# Revit family: QMX_Vertical
name_source: partatom
category: Mechanical Equipment
units: mm (PartAtom-declared; Revit-internal decimal feet)

## family parameters
Always vertical = Yes
Cut with Voids When Loaded = No
Part Type = Normal
Room Calculation Point = No
Round Connector Dimension = Use Radius
Shared = No
Work Plane-Based = No

## types (18) — shared parameters
0 = 0' - 0"
1.5 = 0' - 1 1/2"
1.9375 = 0' - 1 15/16"
3 = 0' - 3"
45 = 45.00°
Manufacturer = Loren Cook Company
Model = QMX-Vertical
ONE EIGTH = 0' - 0 1/8"
Type Comments = Mixed Flow Inline Vertical Mount Belt Drive Arrangement 9
URL = www.lorencook.com

## per-type parameters (varying)
- 90-QMX_VER: (A/2)-.125=0' - 6 9/32"; (F+3)/2=0' - 7 11/16"; (G/2)-.75=0' - 8 7/16"; -(B/2)=-0' - 9 15/16"; -(G/2)-.75=-0' - 8 7/16"; A=1' - 0 13/16"; A/2=0' - 6 13/32"; A/4=0' - 3 7/32"; A/8=0' - 1 19/32"; B=1' - 7 7/8"; B/10=0' - 2"; B/2=0' - 9 15/16"; B/3*2=1' - 1 1/4"; B/6=0' - 3 5/16"; B/8=0' - 3 5/16"; BRACKET=0' - 3"; BRACKET/2=0' - 1 1/2"; C=1' - 3 7/8"; C/2=0' - 7 15/16"; D=0' - 8 1/2"; E=2' - 7 1/4"; E-D=1' - 10 3/4"; E-D-1.5=1' - 9 1/4"; F=1' - 0 3/8"; F+1.5=1' - 1 7/8"; F-1.5=0' - 10 7/8"; F/2=0' - 6 3/16"; G=1' - 6 3/8"; G+1.5=1' - 7 7/8"; G/2=0' - 9 3/16"; H=0' - 0 1/2"; H/2=0' - 0 1/4"; MC/2=0' - 6"; hole=0' - 6 25/32"; hole_dia=1' - 7 3/16"
- 120-QMX_VER: (A/2)-.125=0' - 8 13/32"; (F+3)/2=0' - 9 1/4"; (G/2)-.75=0' - 10 1/2"; -(B/2)=-1' - 0"; -(G/2)-.75=-0' - 10 1/2"; A=1' - 5 1/16"; A/2=0' - 8 17/32"; A/4=0' - 4 9/32"; A/8=0' - 2 1/8"; B=2' - 0"; B/10=0' - 2 13/32"; B/2=1' - 0"; B/3*2=1' - 4"; B/6=0' - 4"; B/8=0' - 4"; BRACKET=0' - 3"; BRACKET/2=0' - 1 1/2"; C=1' - 8 1/16"; C/2=0' - 10 1/32"; D=0' - 10 1/2"; E=3' - 0 11/16"; E-D=2' - 2 3/16"; E-D-1.5=2' - 0 11/16"; F=1' - 3 1/2"; F+1.5=1' - 5"; F-1.5=1' - 2"; F/2=0' - 7 3/4"; G=1' - 10 1/2"; G+1.5=2' - 0"; G/2=0' - 11 1/4"; H=0' - 0 1/2"; H/2=0' - 0 1/4"; MC/2=0' - 8"; hole=0' - 8 11/32"; hole_dia=1' - 11 9/16"
- 135-QMX_VER: (A/2)-.125=0' - 9 1/2"; (F+3)/2=0' - 10 1/4"; (G/2)-.75=1' - 0"; -(B/2)=-1' - 1 1/2"; -(G/2)-.75=-1' - 0"; A=1' - 7 1/4"; A/2=0' - 9 5/8"; A/4=0' - 4 13/16"; A/8=0' - 2 13/32"; B=2' - 3"; B/10=0' - 2 11/16"; B/2=1' - 1 1/2"; B/3*2=1' - 6"; B/6=0' - 4 1/2"; B/8=0' - 4 1/2"; BRACKET=0' - 3"; BRACKET/2=0' - 1 1/2"; C=1' - 10 1/4"; C/2=0' - 11 1/8"; D=1' - 0"; E=3' - 3 1/2"; E-D=2' - 3 1/2"; E-D-1.5=2' - 2"; F=1' - 5 1/2"; F+1.5=1' - 7"; F-1.5=1' - 4"; F/2=0' - 8 3/4"; G=2' - 1 1/2"; G+1.5=2' - 3"; G/2=1' - 0 3/4"; H=0' - 0 1/2"; H/2=0' - 0 1/4"; MC/2=0' - 9"; hole=0' - 9 1/8"; hole_dia=2' - 1 13/16"
- 150-QMX_VER: (A/2)-.125=0' - 10 9/16"; (F+3)/2=0' - 10 7/8"; (G/2)-.75=1' - 1 9/16"; -(B/2)=-1' - 3"; -(G/2)-.75=-1' - 1 9/16"; A=1' - 9 3/8"; A/2=0' - 10 11/16"; A/4=0' - 5 11/32"; A/8=0' - 2 11/16"; B=2' - 6"; B/10=0' - 3"; B/2=1' - 3"; B/3*2=1' - 8"; B/6=0' - 5"; B/8=0' - 5"; BRACKET=0' - 3"; BRACKET/2=0' - 1 1/2"; C=2' - 0 3/8"; C/2=1' - 0 3/16"; D=1' - 1 3/16"; E=3' - 6 1/16"; E-D=2' - 4 7/8"; E-D-1.5=2' - 3 3/8"; F=1' - 6 3/4"; F+1.5=1' - 8 1/4"; F-1.5=1' - 5 1/4"; F/2=0' - 9 3/8"; G=2' - 4 5/8"; G+1.5=2' - 6 1/8"; G/2=1' - 2 5/16"; H=0' - 0 1/2"; H/2=0' - 0 1/4"; MC/2=0' - 10"; hole=0' - 9 29/32"; hole_dia=2' - 4"
- 165-QMX_VER: (A/2)-.125=0' - 11 5/8"; (F+3)/2=0' - 11 29/32"; (G/2)-.75=1' - 3 1/16"; -(B/2)=-1' - 4 1/2"; -(G/2)-.75=-1' - 3 1/16"; A=1' - 11 1/2"; A/2=0' - 11 3/4"; A/4=0' - 5 7/8"; A/8=0' - 2 15/16"; B=2' - 9"; B/10=0' - 3 5/16"; B/2=1' - 4 1/2"; B/3*2=1' - 10"; B/6=0' - 5 1/2"; B/8=0' - 5 1/2"; BRACKET=0' - 3"; BRACKET/2=0' - 1 1/2"; C=2' - 2 1/2"; C/2=1' - 1 1/4"; D=1' - 2 5/16"; E=3' - 7 3/4"; E-D=2' - 5 7/16"; E-D-1.5=2' - 3 15/16"; F=1' - 8 13/16"; F+1.5=1' - 10 5/16"; F-1.5=1' - 7 5/16"; F/2=0' - 10 13/32"; G=2' - 7 5/8"; G+1.5=2' - 9 1/8"; G/2=1' - 3 13/16"; H=0' - 0 1/2"; H/2=0' - 0 1/4"; MC/2=0' - 10"; hole=0' - 10 21/32"; hole_dia=2' - 6 1/8"
- 180-QMX_VER: (A/2)-.125=1' - 0 11/16"; (F+3)/2=1' - 0 29/32"; (G/2)-.75=1' - 4 1/16"; -(B/2)=-1' - 5 1/2"; -(G/2)-.75=-1' - 4 1/16"; A=2' - 1 5/8"; A/2=1' - 0 13/16"; A/4=0' - 6 13/32"; A/8=0' - 3 7/32"; B=2' - 11"; B/10=0' - 3 1/2"; B/2=1' - 5 1/2"; B/3*2=1' - 11 11/32"; B/6=0' - 5 27/32"; B/8=0' - 5 27/32"; BRACKET=0' - 3"; BRACKET/2=0' - 1 1/2"; C=2' - 4 5/8"; C/2=1' - 2 5/16"; D=1' - 3 1/2"; E=3' - 10 1/4"; E-D=2' - 6 3/4"; E-D-1.5=2' - 5 1/4"; F=1' - 10 13/16"; F+1.5=2' - 0 5/16"; F-1.5=1' - 9 5/16"; F/2=0' - 11 13/32"; G=2' - 9 5/8"; G+1.5=2' - 11 1/8"; G/2=1' - 4 13/16"; H=0' - 0 9/16"; H/2=0' - 0 9/32"; MC/2=0' - 10"; hole=0' - 11 7/16"; hole_dia=2' - 8 5/16"
- 202-QMX_VER: (A/2)-.125=1' - 2 1/4"; (F+3)/2=1' - 1 5/8"; (G/2)-.75=1' - 5 5/16"; -(B/2)=-1' - 6 3/4"; -(G/2)-.75=-1' - 5 5/16"; A=2' - 4 3/4"; A/2=1' - 2 3/8"; A/4=0' - 7 3/16"; A/8=0' - 3 19/32"; B=3' - 1 1/2"; B/10=0' - 3 3/4"; B/2=1' - 6 3/4"; B/3*2=2' - 1"; B/6=0' - 6 1/4"; B/8=0' - 6 1/4"; BRACKET=0' - 3"; BRACKET/2=0' - 1 1/2"; C=2' - 7 3/4"; C/2=1' - 3 7/8"; D=1' - 5 1/4"; E=4' - 1 15/16"; E-D=2' - 8 11/16"; E-D-1.5=2' - 7 3/16"; F=2' - 0 1/4"; F+1.5=2' - 1 3/4"; F-1.5=1' - 10 3/4"; F/2=1' - 0 1/8"; G=3' - 0 1/8"; G+1.5=3' - 1 5/8"; G/2=1' - 6 1/16"; H=0' - 0 9/16"; H/2=0' - 0 9/32"; MC/2=0' - 10"; hole=1' - 0 9/16"; hole_dia=2' - 11 1/2"
- 225-QMX_VER: (A/2)-.125=1' - 3 27/32"; (F+3)/2=1' - 2 31/32"; (G/2)-.75=1' - 7 1/16"; -(B/2)=-1' - 8 1/2"; -(G/2)-.75=-1' - 7 1/16"; A=2' - 7 15/16"; A/2=1' - 3 31/32"; A/4=0' - 8"; A/8=0' - 4"; B=3' - 5"; B/10=0' - 4 3/32"; B/2=1' - 8 1/2"; B/3*2=2' - 3 11/32"; B/6=0' - 6 27/32"; B/8=0' - 6 27/32"; BRACKET=0' - 3"; BRACKET/2=0' - 1 1/2"; C=2' - 10 15/16"; C/2=1' - 5 15/32"; D=1' - 7"; E=4' - 7 13/16"; E-D=3' - 0 13/16"; E-D-1.5=2' - 11 5/16"; F=2' - 2 15/16"; F+1.5=2' - 4 7/16"; F-1.5=2' - 1 7/16"; F/2=1' - 1 15/32"; G=3' - 3 5/8"; G+1.5=3' - 5 1/8"; G/2=1' - 7 13/16"; H=0' - 0 9/16"; H/2=0' - 0 9/32"; MC/2=0' - 10 21/32"; hole=1' - 1 11/16"; hole_dia=3' - 2 3/4"
- 245-QMX_VER: (A/2)-.125=1' - 5 1/4"; (F+3)/2=1' - 3 31/32"; (G/2)-.75=1' - 8 13/16"; -(B/2)=-1' - 10 1/4"; -(G/2)-.75=-1' - 8 13/16"; A=2' - 10 3/4"; A/2=1' - 5 3/8"; A/4=0' - 8 11/16"; A/8=0' - 4 11/32"; B=3' - 8 1/2"; B/10=0' - 4 7/16"; B/2=1' - 10 1/4"; B/3*2=2' - 5 21/32"; B/6=0' - 7 13/32"; B/8=0' - 7 13/32"; BRACKET=0' - 3"; BRACKET/2=0' - 1 1/2"; C=3' - 1 3/4"; C/2=1' - 6 7/8"; D=1' - 8 1/2"; E=4' - 11"; E-D=3' - 2 1/2"; E-D-1.5=3' - 1"; F=2' - 4 15/16"; F+1.5=2' - 6 7/16"; F-1.5=2' - 3 7/16"; F/2=1' - 2 15/32"; G=3' - 7 1/8"; G+1.5=3' - 8 5/8"; G/2=1' - 9 9/16"; H=0' - 0 11/16"; H/2=0' - 0 11/32"; MC/2=0' - 11 19/32"; hole=1' - 2 11/16"; hole_dia=3' - 5 9/16"
- 270-QMX_VER: (A/2)-.125=1' - 7 1/32"; (F+3)/2=1' - 5"; (G/2)-.75=1' - 10 1/16"; -(B/2)=-1' - 11 1/2"; -(G/2)-.75=-1' - 10 1/16"; A=3' - 2 5/16"; A/2=1' - 7 5/32"; A/4=0' - 9 19/32"; A/8=0' - 4 25/32"; B=3' - 11"; B/10=0' - 4 11/16"; B/2=1' - 11 1/2"; B/3*2=2' - 7 11/32"; B/6=0' - 7 27/32"; B/8=0' - 7 27/32"; BRACKET=0' - 3"; BRACKET/2=0' - 1 1/2"; C=3' - 5 5/16"; C/2=1' - 8 21/32"; D=1' - 10 7/16"; E=5' - 2 7/8"; E-D=3' - 4 7/16"; E-D-1.5=3' - 2 15/16"; F=2' - 7"; F+1.5=2' - 8 1/2"; F-1.5=2' - 5 1/2"; F/2=1' - 3 1/2"; G=3' - 9 5/8"; G+1.5=3' - 11 1/8"; G/2=1' - 10 13/16"; H=0' - 0 11/16"; H/2=0' - 0 11/32"; MC/2=1' - 0 25/32"; hole=1' - 3 31/32"; hole_dia=3' - 9 1/8"
- 300-QMX_VER: (A/2)-.125=1' - 9 1/8"; (F+3)/2=1' - 6 3/8"; (G/2)-.75=2' - 1 9/16"; -(B/2)=-2' - 3"; -(G/2)-.75=-2' - 1 9/16"; A=3' - 6 1/2"; A/2=1' - 9 1/4"; A/4=0' - 10 5/8"; A/8=0' - 5 5/16"; B=4' - 6"; B/10=0' - 5 13/32"; B/2=2' - 3"; B/3*2=3' - 0"; B/6=0' - 9"; B/8=0' - 9"; BRACKET=0' - 3"; BRACKET/2=0' - 1 1/2"; C=3' - 9 1/2"; C/2=1' - 10 3/4"; D=2' - 0 3/4"; E=5' - 8 1/16"; E-D=3' - 7 5/16"; E-D-1.5=3' - 5 13/16"; F=2' - 9 3/4"; F+1.5=2' - 11 1/4"; F-1.5=2' - 8 1/4"; F/2=1' - 4 7/8"; G=4' - 4 5/8"; G+1.5=4' - 6 1/8"; G/2=2' - 2 5/16"; H=0' - 0 11/16"; H/2=0' - 0 11/32"; MC/2=1' - 2 5/32"; hole=1' - 5 15/32"; hole_dia=4' - 1 3/8"
- 330-QMX_VER: (A/2)-.125=1' - 11 1/4"; (F+3)/2=1' - 7 7/8"; (G/2)-.75=2' - 3 13/16"; -(B/2)=-2' - 5 1/4"; -(G/2)-.75=-2' - 3 13/16"; A=3' - 10 3/4"; A/2=1' - 11 3/8"; A/4=0' - 11 11/16"; A/8=0' - 5 27/32"; B=4' - 10 1/2"; B/10=0' - 5 27/32"; B/2=2' - 5 1/4"; B/3*2=3' - 3"; B/6=0' - 9 3/4"; B/8=0' - 9 3/4"; BRACKET=0' - 3"; BRACKET/2=0' - 1 1/2"; C=4' - 1 3/4"; C/2=2' - 0 7/8"; D=2' - 3"; E=6' - 2 13/16"; E-D=3' - 11 13/16"; E-D-1.5=3' - 10 5/16"; F=3' - 0 3/4"; F+1.5=3' - 2 1/4"; F-1.5=2' - 11 1/4"; F/2=1' - 6 3/8"; G=4' - 9 1/8"; G+1.5=4' - 10 5/8"; G/2=2' - 4 9/16"; H=0' - 0 11/16"; H/2=0' - 0 11/32"; MC/2=1' - 3 19/32"; hole=1' - 6 31/32"; hole_dia=4' - 5 5/8"
- 365-QMX_VER: (A/2)-.125=2' - 1 3/4"; (F+3)/2=1' - 9 3/4"; (G/2)-.75=2' - 6 15/16"; -(B/2)=-2' - 8"; -(G/2)-.75=-2' - 6 15/16"; A=4' - 3 3/4"; A/2=2' - 1 7/8"; A/4=1' - 0 15/16"; A/8=0' - 6 15/32"; B=5' - 4"; B/10=0' - 6 13/32"; B/2=2' - 8"; B/3*2=3' - 6 21/32"; B/6=0' - 10 21/32"; B/8=0' - 10 21/32"; BRACKET=0' - 4"; BRACKET/2=0' - 2"; C=4' - 6 3/4"; C/2=2' - 3 3/8"; D=2' - 5 13/16"; E=6' - 8 1/4"; E-D=4' - 2 7/16"; E-D-1.5=4' - 0 15/16"; F=3' - 4 1/2"; F+1.5=3' - 6"; F-1.5=3' - 3"; F/2=1' - 8 1/4"; G=5' - 3 3/8"; G+1.5=5' - 4 7/8"; G/2=2' - 7 11/16"; H=0' - 0 13/16"; H/2=0' - 0 13/32"; MC/2=1' - 5 1/4"; hole=1' - 9 1/32"; hole_dia=4' - 11 1/2"
- 402-QMX_VER: (A/2)-.125=2' - 4 11/32"; (F+3)/2=1' - 11 1/2"; (G/2)-.75=2' - 9 3/16"; -(B/2)=-2' - 10 1/4"; -(G/2)-.75=-2' - 9 3/16"; A=4' - 8 15/16"; A/2=2' - 4 15/32"; A/4=1' - 2 1/4"; A/8=0' - 7 1/8"; B=5' - 8 1/2"; B/10=0' - 6 27/32"; B/2=2' - 10 1/4"; B/3*2=3' - 9 21/32"; B/6=0' - 11 13/32"; B/8=0' - 11 13/32"; BRACKET=0' - 4"; BRACKET/2=0' - 2"; C=4' - 11 15/16"; C/2=2' - 5 31/32"; D=2' - 8 11/16"; E=7' - 4 5/16"; E-D=4' - 7 5/8"; E-D-1.5=4' - 6 1/8"; F=3' - 8"; F+1.5=3' - 9 1/2"; F-1.5=3' - 6 1/2"; F/2=1' - 10"; G=5' - 7 7/8"; G+1.5=5' - 9 3/8"; G/2=2' - 9 15/16"; H=0' - 0 13/16"; H/2=0' - 0 13/32"; MC/2=1' - 6 31/32"; hole=1' - 10 15/16"; hole_dia=5' - 4 7/8"
- 445-QMX_VER: (A/2)-.125=2' - 7 13/32"; (F+3)/2=2' - 1 5/8"; (G/2)-.75=2' - 11 15/16"; -(B/2)=-3' - 1"; -(G/2)-.75=-2' - 11 15/16"; A=5' - 3 1/16"; A/2=2' - 7 17/32"; A/4=1' - 3 25/32"; A/8=0' - 7 7/8"; B=6' - 2"; B/10=0' - 7 13/32"; B/2=3' - 1"; B/3*2=4' - 1 11/32"; B/6=1' - 0 11/32"; B/8=1' - 0 11/32"; BRACKET=0' - 4"; BRACKET/2=0' - 2"; C=5' - 6 1/16"; C/2=2' - 9 1/32"; D=3' - 0"; E=7' - 10 7/8"; E-D=4' - 10 7/8"; E-D-1.5=4' - 9 3/8"; F=4' - 0 1/4"; F+1.5=4' - 1 3/4"; F-1.5=3' - 10 3/4"; F/2=2' - 0 1/8"; G=6' - 1 3/8"; G+1.5=6' - 2 7/8"; G/2=3' - 0 11/16"; H=0' - 0 13/16"; H/2=0' - 0 13/32"; MC/2=1' - 9 1/32"; hole=2' - 1 1/16"; hole_dia=5' - 10 7/8"
- 490-QMX_VER: (A/2)-.125=2' - 10 9/16"; (F+3)/2=2' - 3 7/8"; (G/2)-.75=3' - 3 3/16"; -(B/2)=-3' - 4 1/4"; -(G/2)-.75=-3' - 3 3/16"; A=5' - 9 3/8"; A/2=2' - 10 11/16"; A/4=1' - 5 11/32"; A/8=0' - 8 11/16"; B=6' - 8 1/2"; B/10=0' - 8 1/16"; B/2=3' - 4 1/4"; B/3*2=4' - 5 21/32"; B/6=1' - 1 13/32"; B/8=1' - 1 13/32"; BRACKET=0' - 4"; BRACKET/2=0' - 2"; C=6' - 0 3/8"; C/2=3' - 0 3/16"; D=3' - 3 7/16"; E=8' - 7 3/8"; E-D=5' - 3 15/16"; E-D-1.5=5' - 2 7/16"; F=4' - 4 3/4"; F+1.5=4' - 6 1/4"; F-1.5=4' - 3 1/4"; F/2=2' - 2 3/8"; G=6' - 7 7/8"; G+1.5=6' - 9 3/8"; G/2=3' - 3 15/16"; H=0' - 0 13/16"; H/2=0' - 0 13/32"; MC/2=1' - 11 1/8"; hole=2' - 3 5/8"; hole_dia=6' - 6 1/8"
- 540-QMX_VER: (A/2)-.125=3' - 2 3/32"; (F+3)/2=2' - 6 1/2"; (G/2)-.75=3' - 6 7/16"; -(B/2)=-3' - 7 1/2"; -(G/2)-.75=-3' - 6 7/16"; A=6' - 4 7/16"; A/2=3' - 2 7/32"; A/4=1' - 7 1/8"; A/8=0' - 9 9/16"; B=7' - 3"; B/10=0' - 8 11/16"; B/2=3' - 7 1/2"; B/3*2=4' - 10"; B/6=1' - 2 1/2"; B/8=1' - 2 1/2"; BRACKET=0' - 4"; BRACKET/2=0' - 2"; C=6' - 7 7/16"; C/2=3' - 3 23/32"; D=3' - 7 5/16"; E=9' - 2 15/16"; E-D=5' - 7 5/8"; E-D-1.5=5' - 6 1/8"; F=4' - 10"; F+1.5=4' - 11 1/2"; F-1.5=4' - 8 1/2"; F/2=2' - 5"; G=7' - 2 3/8"; G+1.5=7' - 3 7/8"; G/2=3' - 7 3/16"; H=0' - 0 13/16"; H/2=0' - 0 13/32"; MC/2=2' - 1 15/32"; hole=2' - 6 1/8"; hole_dia=7' - 1 3/16"
- 600-QMX_VER: (A/2)-.125=3' - 6 5/16"; (F+3)/2=2' - 9 1/2"; (G/2)-.75=3' - 10 11/16"; -(B/2)=-3' - 11 3/4"; -(G/2)-.75=-3' - 10 11/16"; A=7' - 0 7/8"; A/2=3' - 6 7/16"; A/4=1' - 9 7/32"; A/8=0' - 10 5/8"; B=7' - 11 1/2"; B/10=0' - 9 9/16"; B/2=3' - 11 3/4"; B/3*2=5' - 3 21/32"; B/6=1' - 3 29/32"; B/8=1' - 3 29/32"; BRACKET=0' - 4"; BRACKET/2=0' - 2"; C=7' - 3 7/8"; C/2=3' - 7 15/16"; D=4' - 2"; E=10' - 2 1/16"; E-D=6' - 0 1/16"; E-D-1.5=5' - 10 9/16"; F=5' - 4"; F+1.5=5' - 5 1/2"; F-1.5=5' - 2 1/2"; F/2=2' - 8"; G=7' - 10 7/8"; G+1.5=8' - 0 3/8"; G/2=3' - 11 7/16"; H=0' - 0 13/16"; H/2=0' - 0 13/32"; MC/2=2' - 4 9/32"; hole=2' - 9 5/32"; hole_dia=7' - 9 3/4"

## geometry (parser evidence)
native form markers: Sweep x1
no freeform markers — native parametric forms only
